# Revit family: Турникет трипод PERCo_T-5
name_source: partatom
category: Оборудование
units: mm (PartAtom-declared; Revit-internal decimal feet)

## family parameters
Всегда вертикально = Нет
Классификация = Нет
На основе рабочей плоскости = Нет
Общий = Нет
При загрузке вырезать с полостями = Нет
Размер круглого соединителя = Использовать диаметр
Тип детали = Нормальный
Точка расчета площади = Нет

## types (1)
- T-5
    ADSK_URL страницы изделия = https://www.perco.ru
    ADSK_Единица измерения = шт.
    ADSK_Завод-изготовитель = PERCo
    ADSK_Количество = 1
    ADSK_Масса_Текст = не более 22 кг
    ADSK_Материал наименование = Корпус из стали, окрашенной порошковой краской. Планки выполнены из окрашенная сталь, цвет черный муар или из нержавеющей стали.
    ADSK_Наименование = Турникет эл/мех PERCo-T-5
    ADSK_Наименование краткое = Турникет-трипод T-5
    ADSK_Напряжение = 12 В
    ADSK_Номинальная мощность = 9 Вт
    ADSK_Ток = 1 А
    Встраивание считывателей внутрь = Не предусмотрено
    Габаритные размеры (длина×ширина×высота) = 870×836×1026
    Габаритные размеры контроллера для встраивания в нишу = Не предусмотрено
    Габаритные размеры считывателя для встраивания в ниши = Не предусмотрено
    Материал корпуса = Белый
    Материал планки_04 = Нержавейка
    Материал планки_05 = Черный
    Подключение к электросети = 220 В
    Пропускная способность = 30 чел./мин
    Степень защиты оболочки = IP41
    Температура использования = от +1°С до +50°С
    Тип1 = - : PERCo-AS-05
    Цвет = RAL 7032
    Ширина зоны прохода = 500 мм - для планок AS-05, 600 мм - для остальных типов планок
